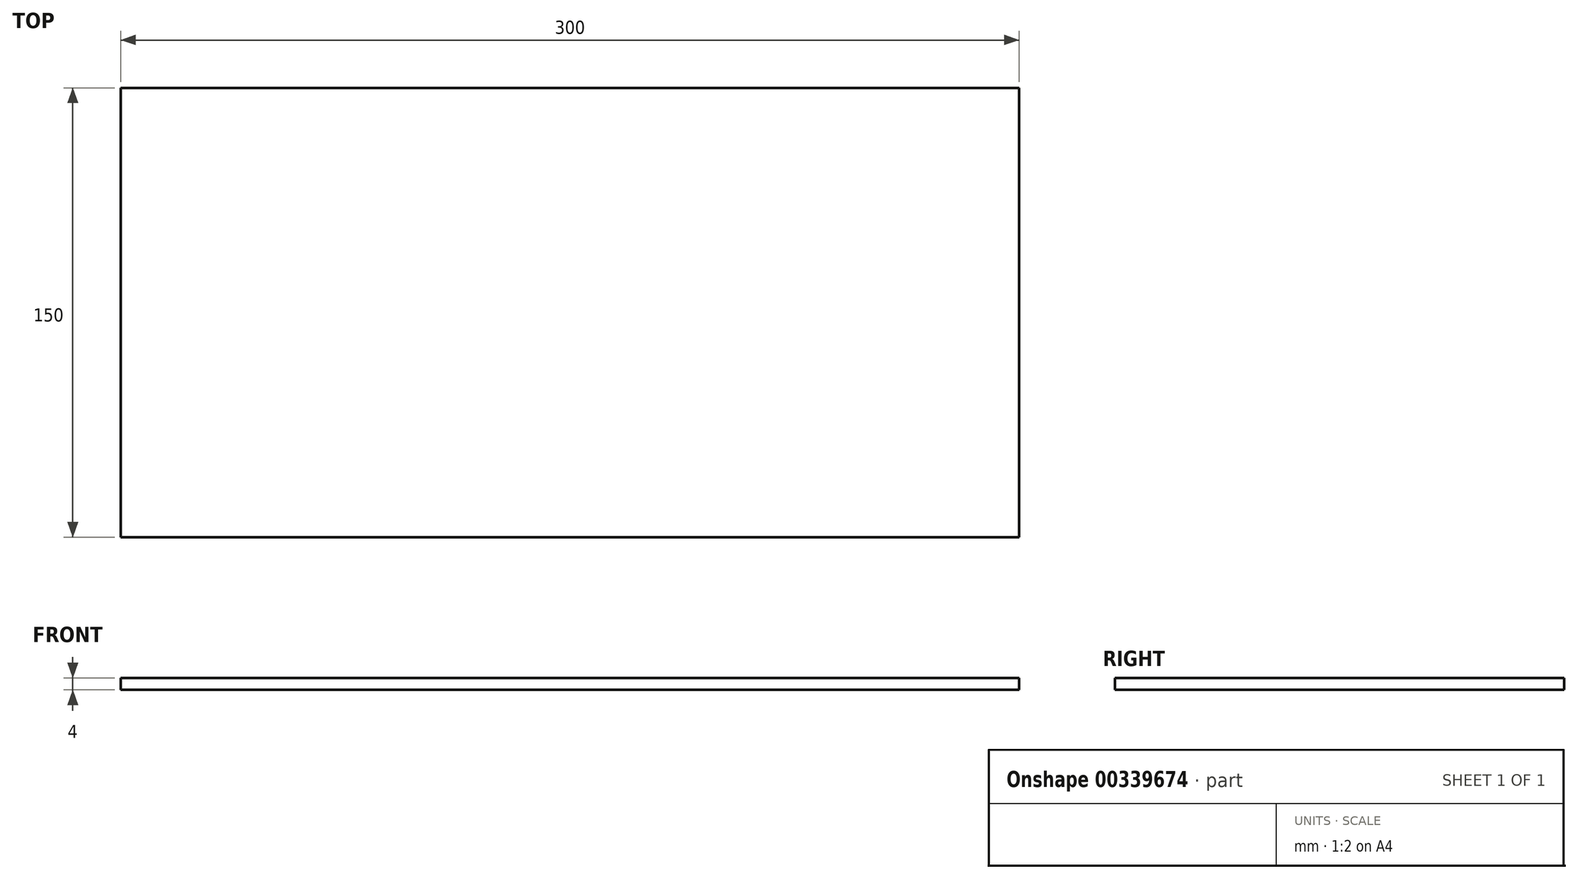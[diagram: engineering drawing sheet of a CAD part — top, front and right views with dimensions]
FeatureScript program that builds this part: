
annotation { "Feature Type Name" : "Feature", "Feature Type Description" : "" }
export const myFeature = defineFeature(function(context is Context, id is Id, definition is map)
    precondition{}
    {
        {
            var Q0;
            Q0=qCreatedBy(makeId("Top.planeOp"),FACE);
            var sketch = newSketch(context, id + "F0", { "sketchPlane" : qUnion([Q0])});
            skLineSegment(sketch, "E0.bottom", {"start": v(0, 0) * mm, "end": v(300, 0) * mm});
            skLineSegment(sketch, "E0.top", {"start": v(0, 150) * mm, "end": v(300, 150) * mm});
            skLineSegment(sketch, "E0.left", {"start": v(0, 0) * mm, "end": v(0, 150) * mm});
            skLineSegment(sketch, "E0.right", {"start": v(300, 0) * mm, "end": v(300, 150) * mm});
            skSolve(sketch);
        }
        {
            var Q0;
            Q0 = qSketchRegion(id + "F0", true);
            extrude(context, id + "F1", {"entities" : qUnion([Q0]), "depth" : 4 * mm});
        }
    });
